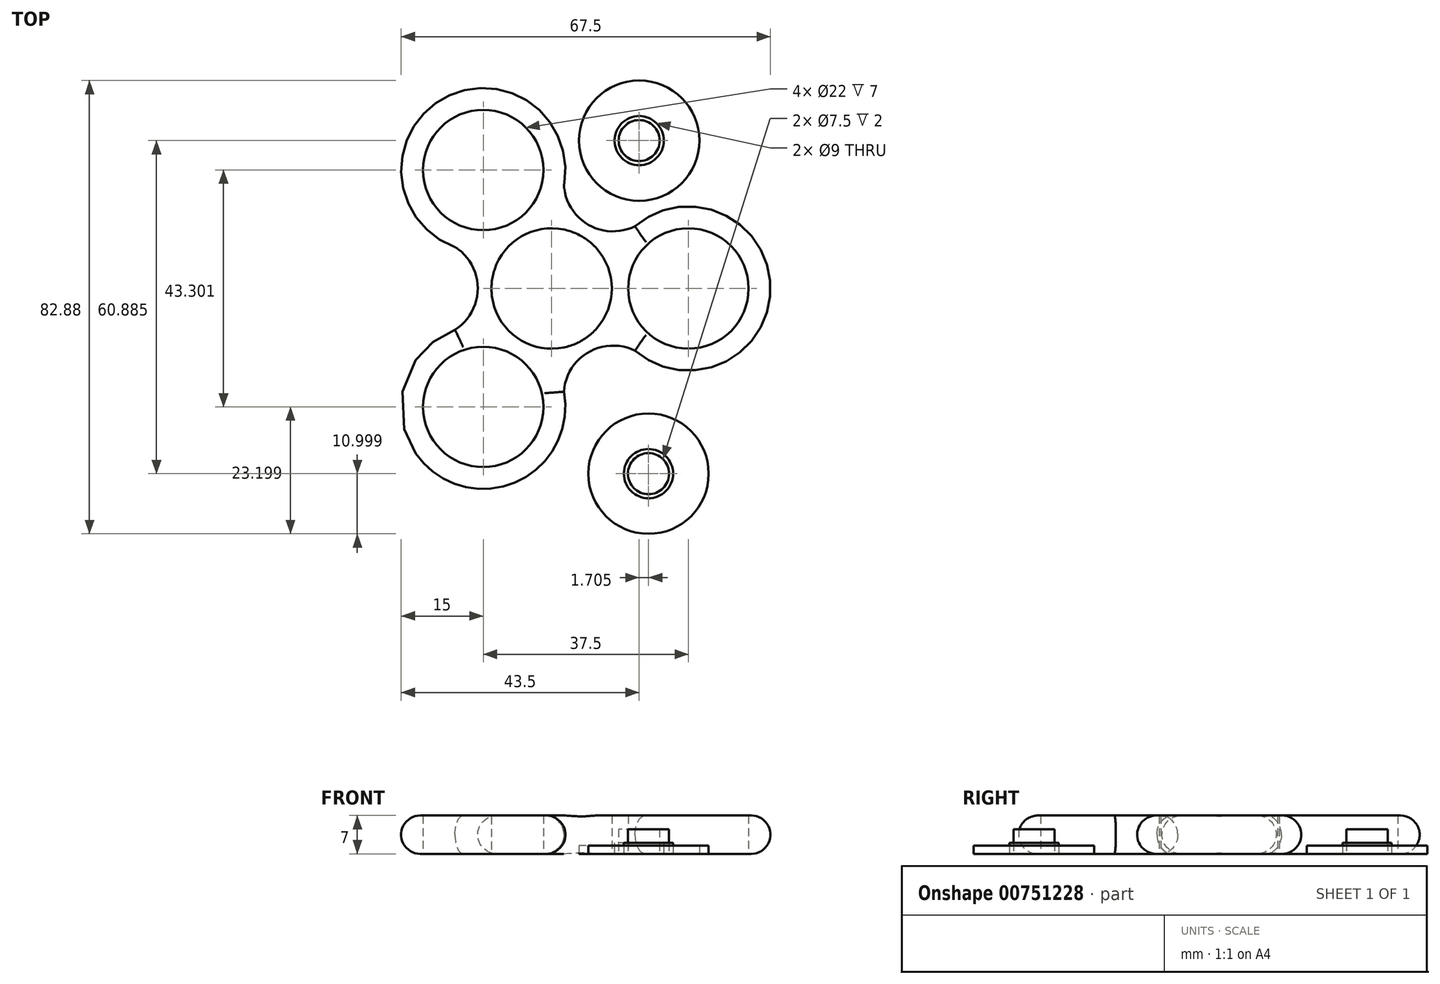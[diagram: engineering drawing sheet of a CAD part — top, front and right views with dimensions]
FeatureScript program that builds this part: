
annotation { "Feature Type Name" : "Feature", "Feature Type Description" : "" }
export const myFeature = defineFeature(function(context is Context, id is Id, definition is map)
    precondition{}
    {
        {
            var Q0;
            Q0=qCreatedBy(makeId("Top.planeOp"),FACE);
            var sketch = newSketch(context, id + "F0", { "sketchPlane" : qUnion([Q0])});
            skCircle(sketch, "E0", {"center": v(0, 0) * mm, "radius": 11 * mm});
            skArc(sketch, "E1.cCircle", {"start": v(-19.87, -8.59) * mm, "mid": v(-19, -10.39) * mm, "end": v(-17.95, -12.1) * mm, "construction": true});
            skLineSegment(sketch, "E1.0", {"start": v(2.5, -21.65) * mm, "end": v(-1.5, -21.65) * mm});
            skLineSegment(sketch, "E1.1", {"start": v(-18, -12.12) * mm, "end": v(-20, -8.66) * mm});
            skLineSegment(sketch, "E1.2", {"start": v(-20, 8.66) * mm, "end": v(-18, 12.12) * mm});
            skLineSegment(sketch, "E1.3", {"start": v(-1.5, 21.65) * mm, "end": v(2.5, 21.65) * mm});
            skLineSegment(sketch, "E1.5", {"start": v(19.5, -9.53) * mm, "end": v(17.5, -13) * mm});
            skPoint(sketch, "E1.0.midPoint", {"position": v(0, -21.65) * mm});
            skCircle(sketch, "E2", {"center": v(-12.5, 21.65) * mm, "radius": 15 * mm});
            skCircle(sketch, "E3", {"center": v(-12.5, 21.65) * mm, "radius": 11 * mm});
            skCircle(sketch, "E4.cCircle", {"center": v(-12.5, 21.65) * mm, "radius": 13 * mm, "construction": true});
            skLineSegment(sketch, "E4.0", {"start": v(-5, 8.66) * mm, "end": v(-20, 8.66) * mm});
            skLineSegment(sketch, "E4.1", {"start": v(-20, 8.66) * mm, "end": v(-27.5, 21.65) * mm});
            skLineSegment(sketch, "E4.2", {"start": v(-27.5, 21.65) * mm, "end": v(-20, 34.64) * mm});
            skLineSegment(sketch, "E4.3", {"start": v(-20, 34.64) * mm, "end": v(-5, 34.64) * mm});
            skLineSegment(sketch, "E4.4", {"start": v(-5, 34.64) * mm, "end": v(2.5, 21.65) * mm});
            skLineSegment(sketch, "E4.5", {"start": v(2.5, 21.65) * mm, "end": v(-5, 8.66) * mm});
            skPoint(sketch, "E4.0.midPoint", {"position": v(-12.5, 8.66) * mm});
            skCircle(sketch, "E5", {"center": v(-12.5, -21.65) * mm, "radius": 15 * mm});
            skCircle(sketch, "E6", {"center": v(-12.5, -21.65) * mm, "radius": 11 * mm});
            skCircle(sketch, "E7.cCircle", {"center": v(-12.5, -21.65) * mm, "radius": 13 * mm, "construction": true});
            skLineSegment(sketch, "E7.0", {"start": v(-5, -34.64) * mm, "end": v(-20, -34.64) * mm});
            skLineSegment(sketch, "E7.1", {"start": v(-20, -34.64) * mm, "end": v(-27.5, -21.65) * mm});
            skLineSegment(sketch, "E7.2", {"start": v(-27.5, -21.65) * mm, "end": v(-20, -8.66) * mm});
            skLineSegment(sketch, "E7.3", {"start": v(-20, -8.66) * mm, "end": v(-5, -8.66) * mm});
            skLineSegment(sketch, "E7.4", {"start": v(-5, -8.66) * mm, "end": v(2.5, -21.65) * mm});
            skLineSegment(sketch, "E7.5", {"start": v(2.5, -21.65) * mm, "end": v(-5, -34.64) * mm});
            skPoint(sketch, "E7.0.midPoint", {"position": v(-12.5, -34.64) * mm});
            skCircle(sketch, "E8", {"center": v(25, 0) * mm, "radius": 15 * mm});
            skCircle(sketch, "E9", {"center": v(25, 0) * mm, "radius": 11 * mm});
            skArc(sketch, "E10.cCircle", {"start": v(13.75, 6.5) * mm, "mid": v(31.5, -11.25) * mm, "end": v(25, 13) * mm, "construction": true});
            skLineSegment(sketch, "E10.0", {"start": v(32.5, -13) * mm, "end": v(17.5, -13) * mm});
            skLineSegment(sketch, "E10.1", {"start": v(17.5, -13) * mm, "end": v(10, 0) * mm});
            skLineSegment(sketch, "E10.2", {"start": v(10, 0) * mm, "end": v(17.5, 13) * mm});
            skLineSegment(sketch, "E10.3", {"start": v(17.5, 13) * mm, "end": v(32.5, 13) * mm});
            skLineSegment(sketch, "E10.4", {"start": v(32.5, 13) * mm, "end": v(40, 0) * mm});
            skLineSegment(sketch, "E10.5", {"start": v(40, 0) * mm, "end": v(32.5, -13) * mm});
            skPoint(sketch, "E10.0.midPoint", {"position": v(25, -13) * mm});
            skPoint(sketch, "E11.orphan", {"position": v(-25, 0) * mm});
            skArc(sketch, "E12.trimOffspring", {"start": v(-1.5, -21.6) * mm, "mid": v(0.5, -21.64) * mm, "end": v(2.5, -21.5) * mm, "construction": true});
            skArc(sketch, "E13.trimOffspring", {"start": v(17.37, -12.92) * mm, "mid": v(18.5, -11.26) * mm, "end": v(19.45, -9.5) * mm, "construction": true});
            skPoint(sketch, "E14.orphan", {"position": v(12.5, -21.65) * mm});
            skPoint(sketch, "E15.orphan", {"position": v(12.5, 21.65) * mm});
            skArc(sketch, "E16", {"start": v(-19.87, -8.59) * mm, "mid": v(-13.5, 0.08) * mm, "end": v(-20, 8.66) * mm});
            skArc(sketch, "E17", {"start": v(17.5, -13) * mm, "mid": v(6.72, -11.65) * mm, "end": v(2.5, -21.65) * mm});
            skArc(sketch, "E18", {"start": v(2.5, 21.65) * mm, "mid": v(6.72, 11.65) * mm, "end": v(17.5, 13) * mm});
            skArc(sketch, "E19.trimOffspring", {"start": v(18.5, 11.25) * mm, "mid": v(18.5, 11.25) * mm, "end": v(18.5, 11.25) * mm, "construction": true});
            skArc(sketch, "E20.trimOffspring", {"start": v(17.35, 12.73) * mm, "mid": v(17.36, 12.82) * mm, "end": v(17.38, 12.92) * mm, "construction": true});
            skSolve(sketch);
        }
        {
            var Q0;
            Q0 = qSketchRegion(id + "F0", true);
            extrude(context, id + "F1", {"entities" : qUnion([Q0]), "depth" : 7 * mm, "offsetDistance" : 25 * mm});
        }
        {
            var Q0;
            Q0=makeQuery(id+"F1.opExtrude","CAP_EDGE",EDGE,{"disambiguationData":[OSD([sQuery(id+"F0.wireOp",EDGE,"E5")])],"isStart":false});
            var Q1;
            Q1=makeQuery(id+"F1.opExtrude","CAP_EDGE",EDGE,{"disambiguationData":[OSD([sQuery(id+"F0.wireOp",EDGE,"E17")])],"isStart":false});
            var Q2;
            Q2=makeQuery(id+"F1.opExtrude","CAP_EDGE",EDGE,{"disambiguationData":[OSD([sQuery(id+"F0.wireOp",EDGE,"E16")])],"isStart":false});
            var Q3;
            Q3=makeQuery(id+"F1.opExtrude","CAP_EDGE",EDGE,{"disambiguationData":[OSD([sQuery(id+"F0.wireOp",EDGE,"E2")])],"isStart":false});
            var Q4;
            Q4=makeQuery(id+"F1.opExtrude","CAP_EDGE",EDGE,{"disambiguationData":[OSD([sQuery(id+"F0.wireOp",EDGE,"E8")])],"isStart":false});
            var Q5;
            Q5=makeQuery(id+"F1.opExtrude","CAP_EDGE",EDGE,{"disambiguationData":[OSD([sQuery(id+"F0.wireOp",EDGE,"E18")])],"isStart":false});
            var Q6;
            Q6=makeQuery(id+"F1.opExtrude","SWEPT_FACE",FACE,{"disambiguationData":[OSD([sQuery(id+"F0.wireOp",EDGE,"E2")])]});
            var Q7;
            Q7=makeQuery(id+"F1.opExtrude","CAP_EDGE",EDGE,{"disambiguationData":[OSD([sQuery(id+"F0.wireOp",EDGE,"E18")])],"isStart":true});
            var Q8;
            Q8=makeQuery(id+"F1.opExtrude","CAP_EDGE",EDGE,{"disambiguationData":[OSD([sQuery(id+"F0.wireOp",EDGE,"E8")])],"isStart":true});
            var Q9;
            Q9=makeQuery(id+"F1.opExtrude","CAP_EDGE",EDGE,{"disambiguationData":[OSD([sQuery(id+"F0.wireOp",EDGE,"E17")])],"isStart":true});
            var Q10;
            Q10=makeQuery(id+"F1.opExtrude","CAP_EDGE",EDGE,{"disambiguationData":[OSD([sQuery(id+"F0.wireOp",EDGE,"E5")])],"isStart":true});
            var Q11;
            Q11=makeQuery(id+"F1.opExtrude","CAP_EDGE",EDGE,{"disambiguationData":[OSD([sQuery(id+"F0.wireOp",EDGE,"E16")])],"isStart":true});
            fillet(context, id + "F2", {"entities" : qUnion([Q0, Q1, Q2, Q3, Q4, Q5, Q6, Q7, Q8, Q9, Q10, Q11]), "radius" : 3.5 * mm, "tangentPropagation" : true, "allowEdgeOverflow" : false});
        }
        {
            var Q0;
            Q0=qCreatedBy(makeId("Top.planeOp"),FACE);
            var sketch = newSketch(context, id + "F3", { "sketchPlane" : qUnion([Q0])});
            skCircle(sketch, "E21", {"center": v(17.7, -33.85) * mm, "radius": 11 * mm});
            skCircle(sketch, "E22", {"center": v(17.7, -33.85) * mm, "radius": 4.5 * mm});
            skCircle(sketch, "E23", {"center": v(17.7, -33.85) * mm, "radius": 3.75 * mm});
            skCircle(sketch, "E24", {"center": v(16, 27.03) * mm, "radius": 11 * mm});
            skCircle(sketch, "E25", {"center": v(16, 27.03) * mm, "radius": 4.5 * mm});
            skCircle(sketch, "E26", {"center": v(16, 27.03) * mm, "radius": 3.75 * mm});
            skSolve(sketch);
        }
        {
            var Q0;
            Q0=makeQuery(id+"F3.imprint","IMPRINT",FACE,{"disambiguationData":[TD([[makeQuery(id+"F3.imprint","IMPRINT",EDGE,{"derivedFrom":sQuery(id+"F3.wireOp",EDGE,"E24")}),1.0]])]});
            var Q1;
            Q1=makeQuery(id+"F3.imprint","IMPRINT",FACE,{"disambiguationData":[TD([[makeQuery(id+"F3.imprint","IMPRINT",EDGE,{"derivedFrom":sQuery(id+"F3.wireOp",EDGE,"E21")}),1.0]])]});
            extrude(context, id + "F4", {"entities" : qUnion([Q0, Q1]), "depth" : 1.5 * mm, "offsetDistance" : 25 * mm});
        }
        {
            var Q0;
            Q0=makeQuery(id+"F3.imprint","IMPRINT",FACE,{"disambiguationData":[TD([[makeQuery(id+"F3.imprint","IMPRINT",EDGE,{"derivedFrom":sQuery(id+"F3.wireOp",EDGE,"E26")}),1.0]])]});
            var Q1;
            Q1=makeQuery(id+"F3.imprint","IMPRINT",FACE,{"disambiguationData":[TD([[makeQuery(id+"F3.imprint","IMPRINT",EDGE,{"derivedFrom":sQuery(id+"F3.wireOp",EDGE,"E23")}),1.0]])]});
            extrude(context, id + "F5", {"entities" : qUnion([Q0, Q1]), "depth" : 4.5 * mm, "offsetDistance" : 25 * mm});
        }
        {
            var Q0;
            Q0=makeQuery(id+"F3.imprint","IMPRINT",FACE,{"disambiguationData":[TD([[makeQuery(id+"F3.imprint","IMPRINT",EDGE,{"derivedFrom":sQuery(id+"F3.wireOp",EDGE,"E25")}),1.0]])]});
            var Q1;
            Q1=makeQuery(id+"F3.imprint","IMPRINT",FACE,{"disambiguationData":[TD([[makeQuery(id+"F3.imprint","IMPRINT",EDGE,{"derivedFrom":sQuery(id+"F3.wireOp",EDGE,"E22")}),1.0]])]});
            extrude(context, id + "F6", {"entities" : qUnion([Q0, Q1]), "depth" : 2 * mm, "offsetDistance" : 25 * mm});
        }
    });
